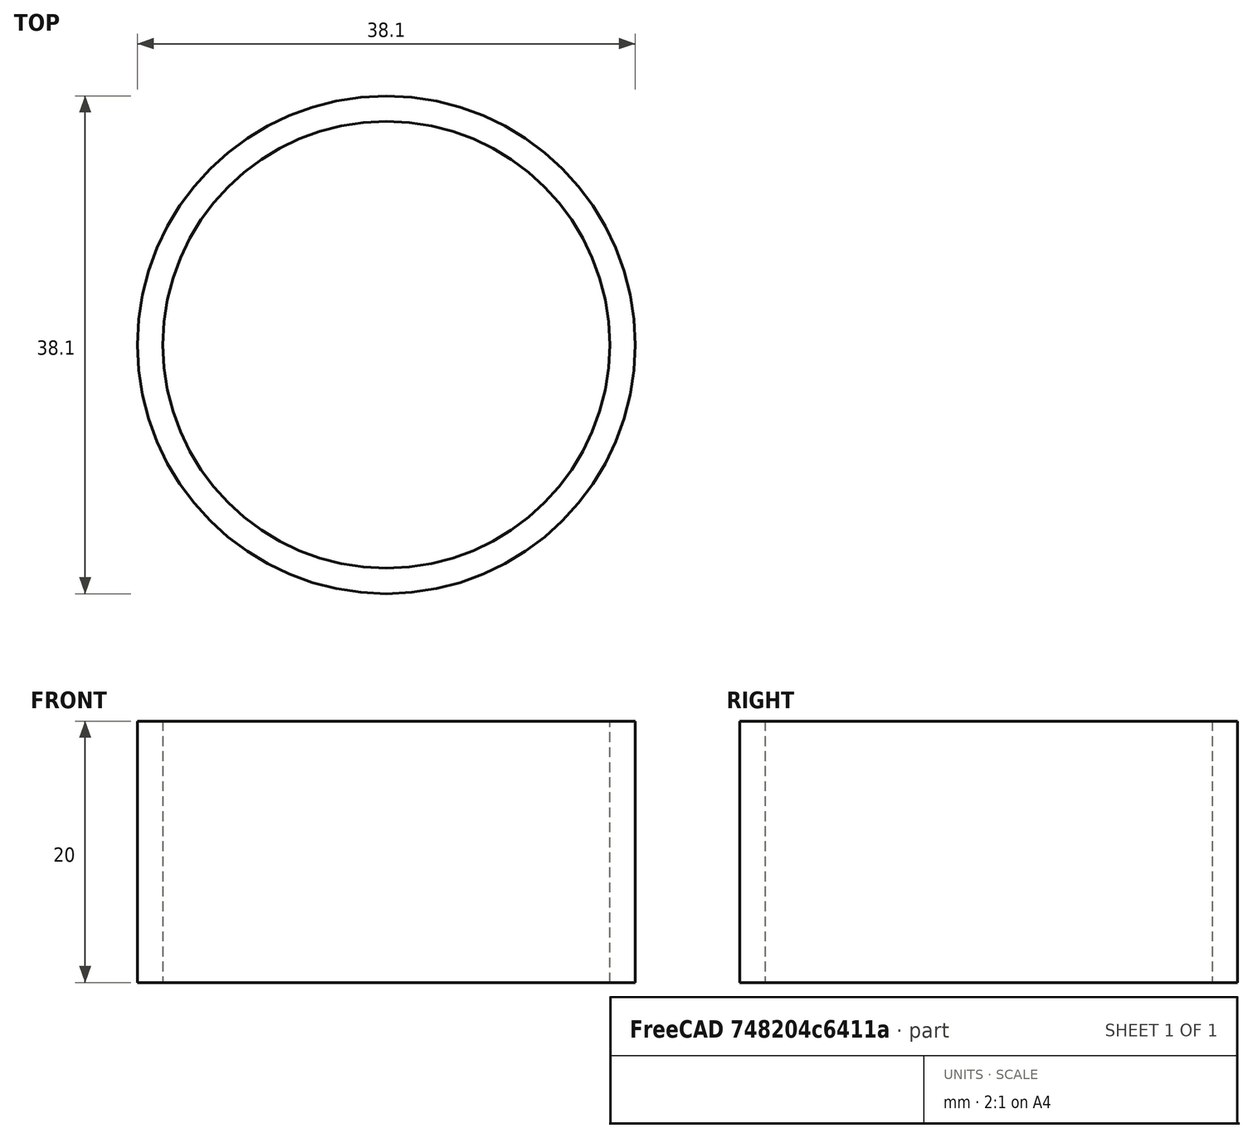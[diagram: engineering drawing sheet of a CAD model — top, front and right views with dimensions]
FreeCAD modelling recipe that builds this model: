
FCSTD DOCUMENT  (FreeCAD 0.20R29177 +426 (Git))
Label: PillowSpindleSpacer
License: All rights reserved
LicenseURL: http://en.wikipedia.org/wiki/All_rights_reserved
objects: Sketcher::SketchObject×1, PartDesign::Pad×1, PartDesign::Body×1
note: 4 computed .brp shape members not serialized (recipe doc carries the construction recipe); baked Part::Feature solids carry a one-line shape summary decoded from their .brp

FEATURE [Sketcher::SketchObject] Sketch
  FullyConstrained = true
  MapMode = 5
  Support = -> [XY_Plane]
  sketch-geometry (2):
    g0: Circle CenterX=0 CenterY=0 CenterZ=0 NormalX=0 NormalY=0 NormalZ=1 AngleXU=0 Radius=17.1
    g1: Circle CenterX=0 CenterY=0 CenterZ=0 NormalX=0 NormalY=0 NormalZ=1 AngleXU=0 Radius=19.05
  constraints (4):
    c: Coincident(g0,g-1)
    c: Coincident(g1,g0)
    c: Diameter(g0) = 34.2
    c: Diameter(g1) = 38.1
FEATURE [PartDesign::Pad] Pad
  Direction = (0,0,1)
  Length = 20
  Length2 = 10
  Profile = -> Sketch
  ReferenceAxis = -> Sketch [N_Axis]
  Type = 0
FEATURE [PartDesign::Body] Body
  Group = -> [Sketch,Pad]
  Origin = -> Origin
  Tip = -> Pad
